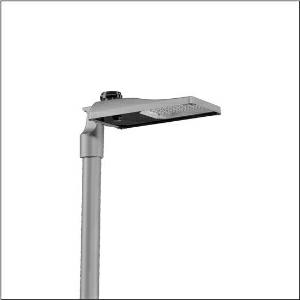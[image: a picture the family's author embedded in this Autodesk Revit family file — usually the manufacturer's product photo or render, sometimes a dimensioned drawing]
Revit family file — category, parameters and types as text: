
# Revit family: streetlight_sl_31_mini___st1_0a_5xh6d3bm08ja_37c8
name_source: partatom
category: Lighting Fixtures
units: mm (PartAtom-declared; Revit-internal decimal feet)

## family parameters
Cut with Voids When Loaded = No
Host = Face
Light Source = No
Part Type = Normal
Room Calculation Point = No
Round Connector Dimension = Use Diameter
Shared = No

## types (1)
- --- (1 x LED, 12270 lm, 82.5 W, 3000K)
    Apparent Load = 83 VA
    CIE Flux Codes = 40 73 97 100 100
    Color Rendering = 70
    Color Temperature = 3000K
    Default Elevation = 1800 mm
    Description = Streetlight SL 31 mini NEMA (7pin) mast luminaire for post-top, side-entry; light control with lens of PMMA; light distribution: ST1.0a, direct asymmetric distribution, for standard-compliant lighting for roads and squares; LED: luminous flux: 12.270lm, light colour: 730, colour temperature: 3000K; luminous efficacy: 148,7lm/W; control: pre-setting: linear dimming characteristic, flexible luminous flux parameterisation, time-dependent luminous flux control, constant luminous flux control, intelligent temperature release in ECG and LED module, overheat protection; luminaire housing, of diecast aluminium, Siteco® metallic grey (DB 702S), corrosivity category C5 high according to DIN EN ISO 12944; cover of toughened safety glass, transparent, opened without tools; mast flange of diecast aluminium, Siteco® metallic grey (DB 702S), spigot size: 76/60mm, mast flange included unmounted; with cable H07RN-F 3x 1.5mm², cable length: 10,5m, connection cable pre-assembled; mains connection: 220..240V, AC, 50/60Hz; power consumption (at start of service life): 82,5W / (at end of service life): 90,1W / (with reduced operation 50%): 36,8W; protection rating (complete): IP66; insulation class (complete): insulation class I (protective earthing); impact resistance: IK09; certification: CE, ENEC, ENEC+, VDE, UKCA; permissible operating ambient temperature for outdoor applications: -40..+50°C; packaging unit: 1 piece

Light Distribution: ST1.0a
    Height = 76 mm
    Lamp = 1 x LED
    Lamp Light Flux = 12270 lm
    Lamp Power = 82.5 W
    Lamp count = 1
    Length = 547 mm
    Luminous efficacy = 149 lm/W
    Manufacturer = Siteco
    ModVariant = No
    Model = 5XH6D3BM08JA
    Number of Poles = 1
    OnlyDefault = Yes
    Power Factor = 1
    Product Name = Streetlight SL 31 mini | ST1.0a
    Product group = mast luminaire | pylon top
    ProductGroupID = 6100
    Protection Class = Protection class I
    Protection Degree = IP 66
    RLX_Detail_Level = 1
    RLX_Emergency_Light_Flux = 0 lm
    RLX_Emergency_Type = 0
    RLX_Emergency_Type_DB = No
    RlxData = <blob elided: 40313 chars, md5=c0f896ca>
    Socket = socket
    Standby Power = 0 W
    System Light Flux = 12270 lm
    System Power = 83 W
    Type Comments = factory setting: luminous flux: 100 % | dim-lin: 254 | 870 mA
    Type Image = l_1300324.jpg
    URL = http://relux.com
    VarID = @adj_050006
    Voltage = 0 V
    Weight = 0.00 kg
    Width = 265 mm

## geometry (parser evidence)
native form markers: Blend x4, Sweep x9
no freeform markers — native parametric forms only
